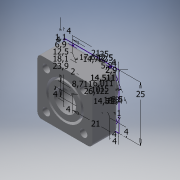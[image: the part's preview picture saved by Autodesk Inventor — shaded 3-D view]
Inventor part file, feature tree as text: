
AUTODESK INVENTOR PART (.ipt)
format: ipt  version: 2019 (Build 230136000, 136)  size: 309,760 bytes
history: native  units: mm
features: extrude x10, other x3, sketch x1, plane x1, loft x1, hole x1, fillet x1
ambient origin geometry x8: Origin, YZ Plane, XZ Plane, XY Plane, X Axis, Y Axis, Z Axis, Center Point
bodies: Volumenkörper1 (feature_tree), Volumenkörper2 (feature_tree), Volumenkörper3 (feature_tree), Volumenkörper7 (feature_tree), Volumenkörper9 (feature_tree)
feature tree (18):
  sketch  "Skizze1"  dims[d35=4.0mm d36=0.0mm d48=25.0mm d49=25.0mm d50=4.0mm d51=4.0mm d52=4.0mm d53=10.0mm d54=1.0mm d55=15.0mm d57=12.0mm d58=0.0mm d59=12.0mm d60=0.0mm d61=-8.0mm d72=20.0mm d73=0.0mm d78=0.0mm d79=90.0deg d80=0.0mm d81=90.0deg d96=3.4mm d97=8.0mm d98=6.5mm d99=3.4mm d100=90.0deg d101=8.0mm d102=20.594885mm d103=4.0mm d104=4.0mm d105=4.0mm d106=4.0mm d158=5.0mm d159=0.0mm d160=5.0mm d161=0.0mm d162=2.0mm d167=2.0mm d168=8.5mm d169=5.8mm d170=14.3mm d171=14.722432mm d172=1.1mm d173=6.9mm d174=18.1mm d175=23.9mm d176=12.5mm d177=14.511216mm d178=6.011216mm d179=14.511216mm d180=12.5mm d181=8.711216mm d182=2.9mm d183=4.0mm d184=2.9mm d185=4.0mm d186=11.4mm d187=12.5mm d188=14.511216mm d189=21.0mm d190=17.622432mm d191=21.0mm d192=26.122432mm d193=3.0mm d194=0.0mm d195=3.0mm d196=0.0mm d197=3.0mm d198=0.0mm d199=3.0mm d200=0.0mm]
  extrude  "Extrusion1"  Depth=25.0mm
  extrude  "Extrusion2"  Depth=25.0mm
  extrude  "Extrusion3"  Depth=4.0mm
  plane  "Arbeitsebene1"
  extrude  "Extrusion7"  Depth=4.0mm
  loft  "Erhebung3"
  other  "Kombinieren1"
  hole  "Bohrung3"  [1 undecoded]
  extrude  "Extrusion12"  Depth=1.0mm
  extrude  "Extrusion13"  Depth=3.0mm
  fillet  "Rundung1"  Radius=12.0mm
  extrude  "Extrusion14"  Depth=12.0mm TaperAngle=0.0deg
  extrude  "Extrusion15"  [1 undecoded]
  extrude  "Extrusion16"  Depth=3.0mm TaperAngle=0.0deg
  extrude  "Extrusion17"  TaperAngle=0.0deg  [1 undecoded]
  other  "Kanten5"
  other  "Kanten6"
note: 3 required parameter values undecoded (feature->parameter linkage not recoverable at this tier; creation-order binding heuristic only, values carry confidence <= 0.55)
